# Revit family: NAU_Naughtone_Stng_Always
name_source: partatom
category: Generic Models
revit_build: Autodesk Revit 2018 (Build: 20170223_1515(x64)
units: mm (PartAtom-declared; Revit-internal decimal feet)

## family parameters
Always vertical = Yes
Can host rebar = No
Cut with Voids When Loaded = No
OmniClass Number = 23.40.00.00
OmniClass Title = Equipment and Furnishings
Part Type = Normal
Room Calculation Point = No
Round Connector Dimension = Use Diameter
Shared = No
Work Plane-Based = No

## types (6) — shared parameters
Assembly Code = E2020200
AssetType = Movable
BIMObjectName = NAU_Naughtone_Seating_Always
Category = Pr_40_50_12 : Chairs, seats and benches
Color = Various
DurationUnit = year
HighestSeatingHeight = 470 mm  [stored 1.54199 ft]
IfcExportAs = IfcFurnishingElementType
IfcExportType = CHAIR
Keynote = Pr_40_50_12
LowestSeatingHeight = 470 mm  [stored 1.54199 ft]
MainColor = Various
ManufacturerAddress = Knaresborough Tech Park, Manse Lane, Knaresborough, HG5 8LF
ManufacturerName = Naughtone
ManufacturerURL = www.naughtone.com
NBSDescription = Seating
NBSReference = 45-35-72/352
Name = Seating_Always_Naughtone
NominalHeight = 780 mm  [stored 2.55906 ft]
NominalWidth = 595 mm  [stored 1.9521 ft]
ProductInformation = www.naughtone.com/products/always/
ReplacementCost = 0.00
Revision = 2
SeatingHeight = 470 mm  [stored 1.54199 ft]
Shape = Rectangular
SustainabilityPerformance = FISP certified. ISO 14001. SCS indoor advantage gold
URL = www.naughtone.com
Uniclass2015Code = Pr_40_50_12
Uniclass2015Title = Chairs, seats and benches
Version = 1
WarrantyDescription = Request warranty information from naughtone
WarrantyDurationLabor = 7
WarrantyDurationParts = 7
WarrantyDurationUnit = year

## per-type parameters (varying)
| type | Description | Has4LegBase | Has4StarBase | Has5StarBase | HasCantileverBase | HasSledBase | HasSwivelBase | HasWoodBase | Model | ModelNumber | ModelReference | NominalLength | Size |
| ALCHBST4 - Always Chair on 4 Leg Base | Always Chair on 4 Leg Base | Yes | No | No | No | No | No | No | ALCHBST4 | ALCHBST4 | Always Chair on 4 Leg Base | 625 mm  [stored 2.05052 ft] | 625 x 595 x 780mm |
| ALCHBSL - Always Chair Sled Base | Always Chair on Sled Base | No | No | No | No | Yes | No | No | ALCHBSL | ALCHBSL | Always Chair on Sled Base | 625 mm  [stored 2.05052 ft] | 625 x 595 x 780mm |
| ALCHBCL - Always Chair on Cantilever Base | Always Chair on Cantilever Base | No | No | No | Yes | No | No | No | ALCHBCL | ALCHBCL | Always Chair on Cantilever Base | 625 mm  [stored 2.05052 ft] | 625 x 595 x 780mm |
| ALCHBWD - Always Chair on Wooden Base | Always Chair on Wooden Base | No | No | No | No | No | No | Yes | ALCHBWD | ALCHBWD | Always Chair on Wooden Base | 625 mm  [stored 2.05052 ft] | 625 x 595 x 780mm |
| ALCHB4S - Always Chair with 4 Star base | Always Chair with 4 Star base | No | Yes | No | No | No | Yes | No | ALCHB4S | ALCHB4S | Always Chair with 4 Star base | 625 mm  [stored 2.05052 ft] | 625 x 595 x 780mm |
| ALCHB5S - Always Chair with 5 Star base | Always Chair with 5 Star base | No | No | Yes | No | No | Yes | No | ALCHB5S | ALCHB5S | Always Chair with 5 Star base | 635 mm | 635 x 595 x 780mm |

note: [stored X ft] marks values corroborated as IEEE doubles in the binary element streams (Revit-internal decimal feet)

## geometry (parser evidence)
native form markers: Blend x2, Sweep x2
no freeform markers — native parametric forms only
